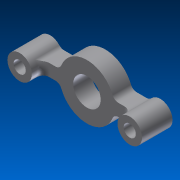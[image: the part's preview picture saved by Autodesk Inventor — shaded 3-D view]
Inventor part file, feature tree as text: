
AUTODESK INVENTOR PART (.ipt)
format: ipt  version: 2012 (Build 160160000, 160)  size: 127,488 bytes
history: native  units: in
note: dims shown in document units (in); Inventor stores cm internally (conversion verified against a paired STEP export)
features: fillet x1, other x1, imported_body x1
ambient origin geometry x8: Origin, YZ Plane, XZ Plane, XY Plane, X Axis, Y Axis, Z Axis, Center Point
feature tree (3):
  fillet  "Redondeo2"  [1 undecoded]
  other  "Pieza chica1"
  imported_body  "Base1"
note: 1 required parameter value undecoded (feature->parameter linkage not recoverable at this tier; creation-order binding heuristic only, values carry confidence <= 0.55)
